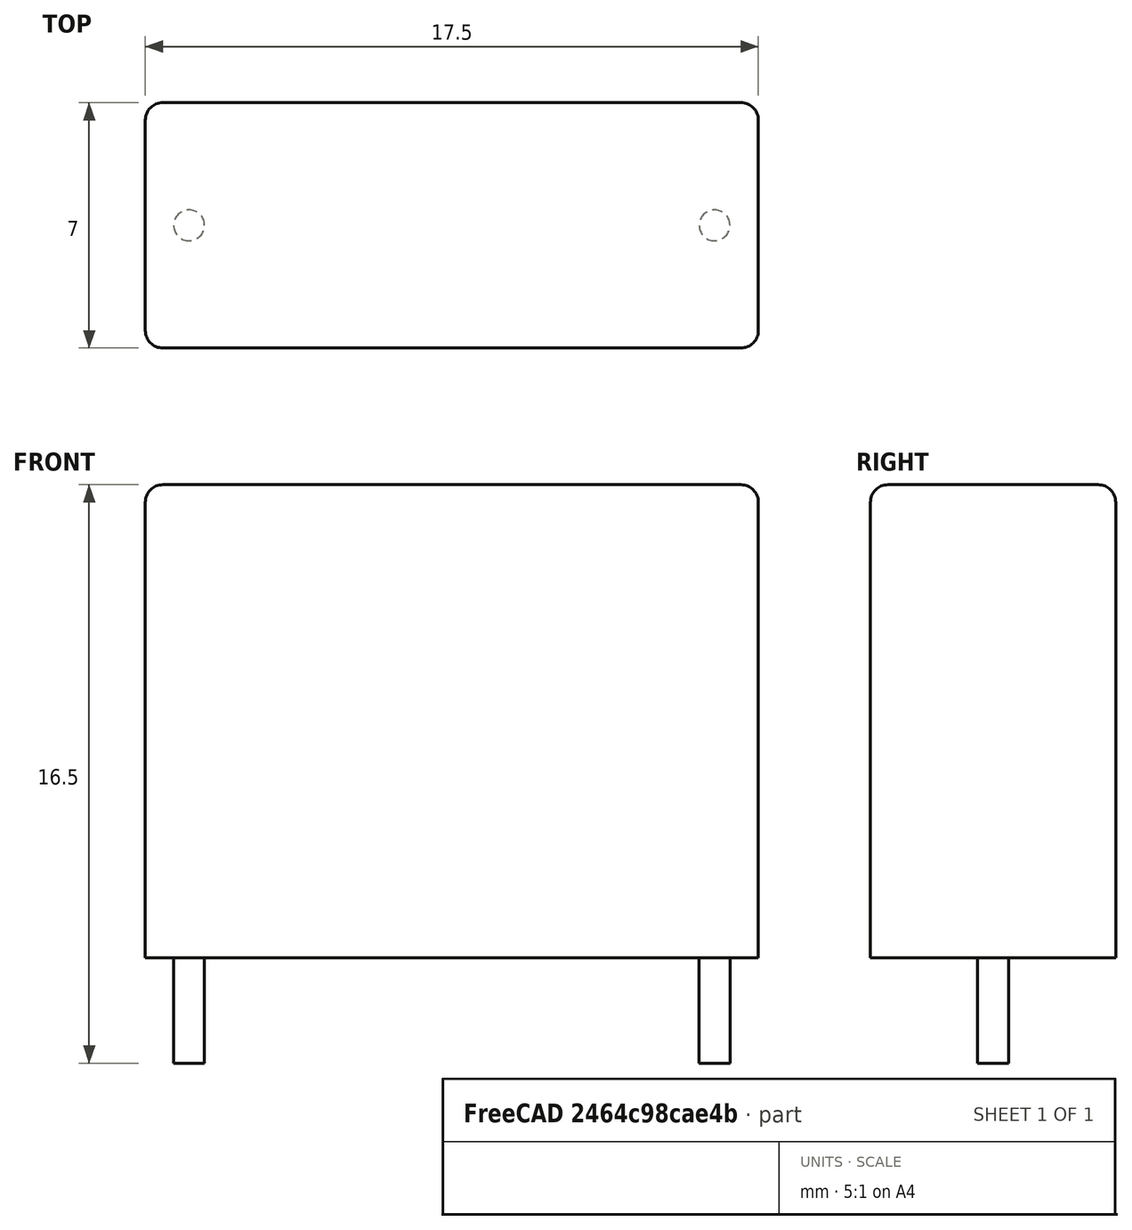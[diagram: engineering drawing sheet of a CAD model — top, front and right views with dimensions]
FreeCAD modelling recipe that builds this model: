
FCSTD DOCUMENT
Label: CAPARV1500W80L1750T700H1350
objects: Part::Cylinder×2, Part::Fuse×2, Part::Box×1, Part::Fillet×1
note: 6 computed .brp shape members not serialized (recipe doc carries the construction recipe); baked Part::Feature solids carry a one-line shape summary decoded from their .brp

FEATURE [Part::Cylinder] Cylinder  label="Pin1"
  Angle = 360
  Height = 3
  Placement = pos=(-7.5,0,-3) rot=(0,0,1;0rad)
  Radius = 0.44
FEATURE [Part::Cylinder] Cylinder001  label="Pin2"
  Angle = 360
  Height = 3
  Placement = pos=(7.5,0,-3) rot=(0,0,1;0rad)
  Radius = 0.44
FEATURE [Part::Box] Box  label="Grundkoerper"
  Height = 13.5
  Length = 17.5
  Placement = pos=(-8.75,-3.5,0) rot=(0,0,1;0rad)
  Width = 7
FEATURE [Part::Fillet] Fillet
  Base = -> Box
  Edges = 8 edges r=0.5: [Edge1,Edge2,Edge3,Edge5,Edge6,Edge7,Edge10,Edge12]
FEATURE [Part::Fuse] Fusion
  Base = -> Fillet
  Tool = -> Cylinder
FEATURE [Part::Fuse] Fusion001  label="CAPARV1500W80L1750T700H1350"
  Base = -> Fusion
  Tool = -> Cylinder001
